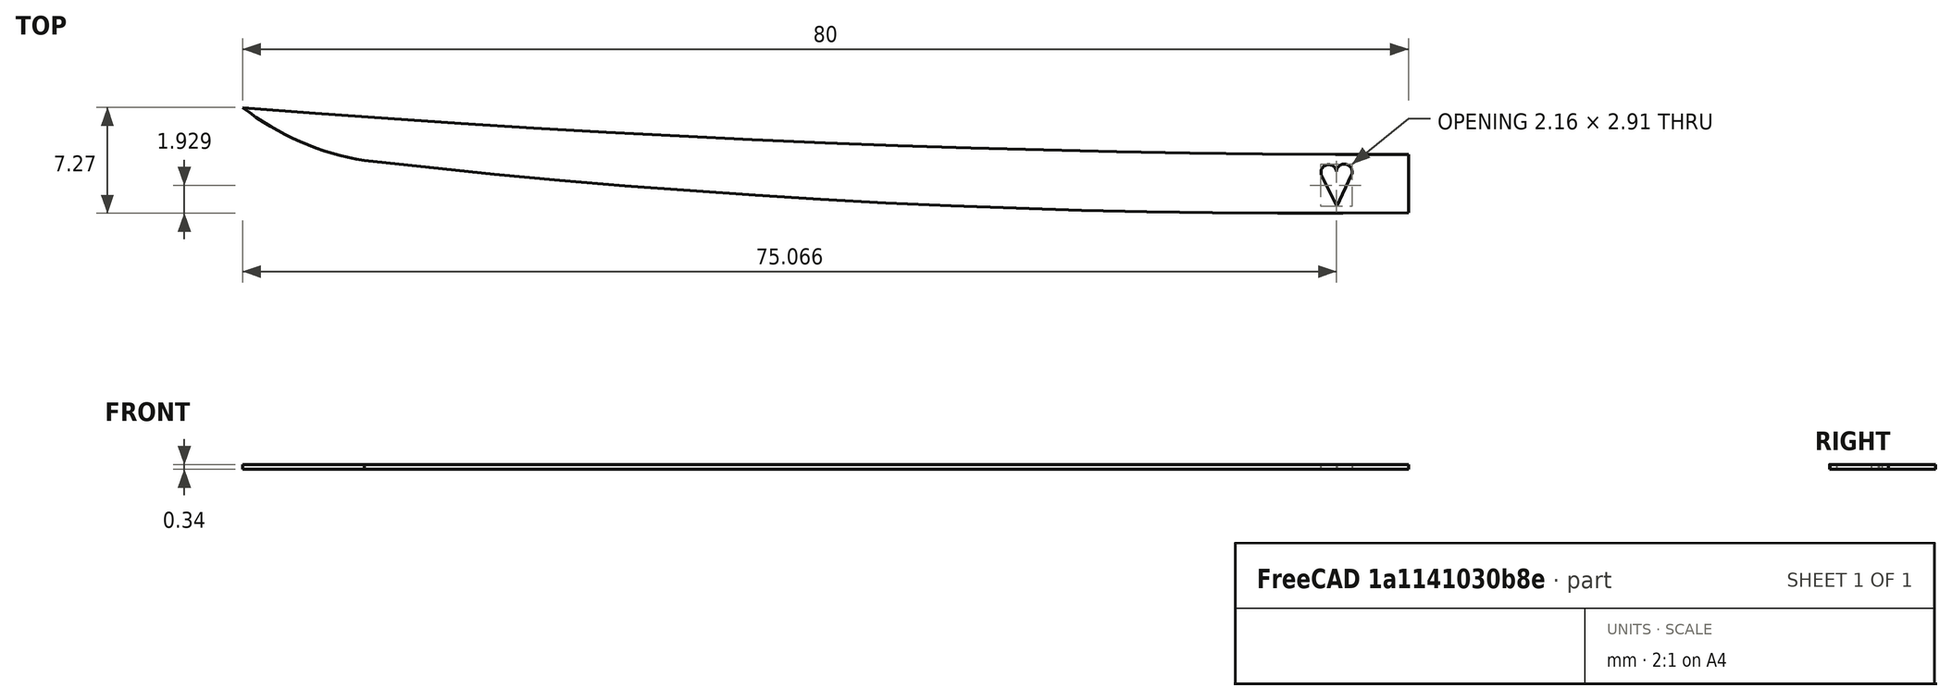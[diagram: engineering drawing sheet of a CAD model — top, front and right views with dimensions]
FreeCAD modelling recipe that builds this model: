
FCSTD DOCUMENT  (FreeCAD 0.20R29410 (Git))
Label: lamina
License: All rights reserved
LicenseURL: http://en.wikipedia.org/wiki/All_rights_reserved
objects: Sketcher::SketchObject×2, PartDesign::Pad×1, PartDesign::Pocket×1, PartDesign::Body×1
note: 7 computed .brp shape members not serialized (recipe doc carries the construction recipe); baked Part::Feature solids carry a one-line shape summary decoded from their .brp

FEATURE [Sketcher::SketchObject] Sketch
  FullyConstrained = false
  MapMode = 5
  Support = -> [XY_Plane]
  sketch-geometry (4):
    g0: LineSegment StartX=1.696e-13 StartY=-4 StartZ=0 EndX=1.696e-13 EndY=0 EndZ=0
    g1: ArcOfCircle CenterX=8.14529e-06 CenterY=993.472 CenterZ=0 NormalX=0 NormalY=0 NormalZ=1 AngleXU=0 Radius=993.472 StartAngle=4.63178 EndAngle=4.71239
    g2: ArcOfCircle CenterX=-6.84281 CenterY=577.149 CenterZ=0 NormalX=0 NormalY=0 NormalZ=1 AngleXU=0 Radius=581.189 StartAngle=4.60066 EndAngle=4.72416
    g3: ArcOfCircle CenterX=-68.6243 CenterY=17.9161 CenterZ=0 NormalX=0 NormalY=0 NormalZ=1 AngleXU=0 Radius=18.5795 StartAngle=4.05346 EndAngle=4.54919
  constraints (8):
    c: DistanceY(g0,g0) = 4
    c: Vertical(g0)
    c: Coincident(g-1,g0)
    c: Coincident(g1,g0)
    c: Coincident(g2,g0)
    c: Coincident(g3,g1)
    c: Coincident(g3,g2)
    c: Block(g1)
FEATURE [PartDesign::Pad] Pad
  Direction = (0,0,1)
  Length = 0.34
  Length2 = 10
  Profile = -> Sketch
  ReferenceAxis = -> Sketch [N_Axis]
  Refine = true
  Type = 0
FEATURE [Sketcher::SketchObject] Sketch001
  FullyConstrained = false
  MapMode = 5
  Placement = pos=(0,0,0.34) rot=(0,0,1;0rad)
  Support = -> [Pad]
  sketch-geometry (8):
    g0: LineSegment StartX=28.6258 StartY=-25.954 StartZ=0 EndX=28.7824 EndY=-25.954 EndZ=0
    g1: LineSegment StartX=28.7824 StartY=-25.954 StartZ=0 EndX=28.7824 EndY=-26.1034 EndZ=0
    g2: LineSegment StartX=28.7824 StartY=-26.1034 StartZ=0 EndX=28.6258 EndY=-26.1034 EndZ=0
    g3: LineSegment StartX=28.6258 StartY=-26.1034 StartZ=0 EndX=28.6258 EndY=-25.954 EndZ=0
    g4: ArcOfCircle CenterX=-5.47143 CenterY=-1.23182 CenterZ=0 NormalX=0 NormalY=0 NormalZ=1 AngleXU=0 Radius=0.532669 StartAngle=0.0923273 EndAngle=3.60569
    g5: LineSegment StartX=-4.91192 StartY=-3.53959 StartZ=0 EndX=-3.91635 EndY=-1.42204 EndZ=0
    g6: LineSegment StartX=-4.91192 StartY=-3.53959 StartZ=0 EndX=-5.94776 EndY=-1.47025 EndZ=0
    g7: ArcOfCircle CenterX=-4.40318 CenterY=-1.19315 CenterZ=0 NormalX=0 NormalY=0 NormalZ=1 AngleXU=0 Radius=0.537954 StartAngle=5.8437 EndAngle=9.40537
  constraints (12):
    c: Coincident(g0,g1)
    c: Coincident(g1,g2)
    c: Coincident(g2,g3)
    c: Coincident(g3,g0)
    c: Horizontal(g0)
    c: Horizontal(g2)
    c: Vertical(g1)
    c: Vertical(g3)
    c: Tangent(g5,g7) = -1.5708
    c: Tangent(g6,g4) = 1.5708
    c: Coincident(g7,g4)
    c: Coincident(g6,g5)
FEATURE [PartDesign::Pocket] Pocket
  BaseFeature = -> Pad
  Direction = (0,0,-1)
  Length = 5
  Length2 = 5
  Profile = -> Sketch001
  ReferenceAxis = -> Sketch001 [N_Axis]
  Refine = true
  TaperAngle = 2
  Type = 0
FEATURE [PartDesign::Body] Body
  Group = -> [Sketch,Pad,Sketch001,Pocket]
  Origin = -> Origin
  Tip = -> Pocket
